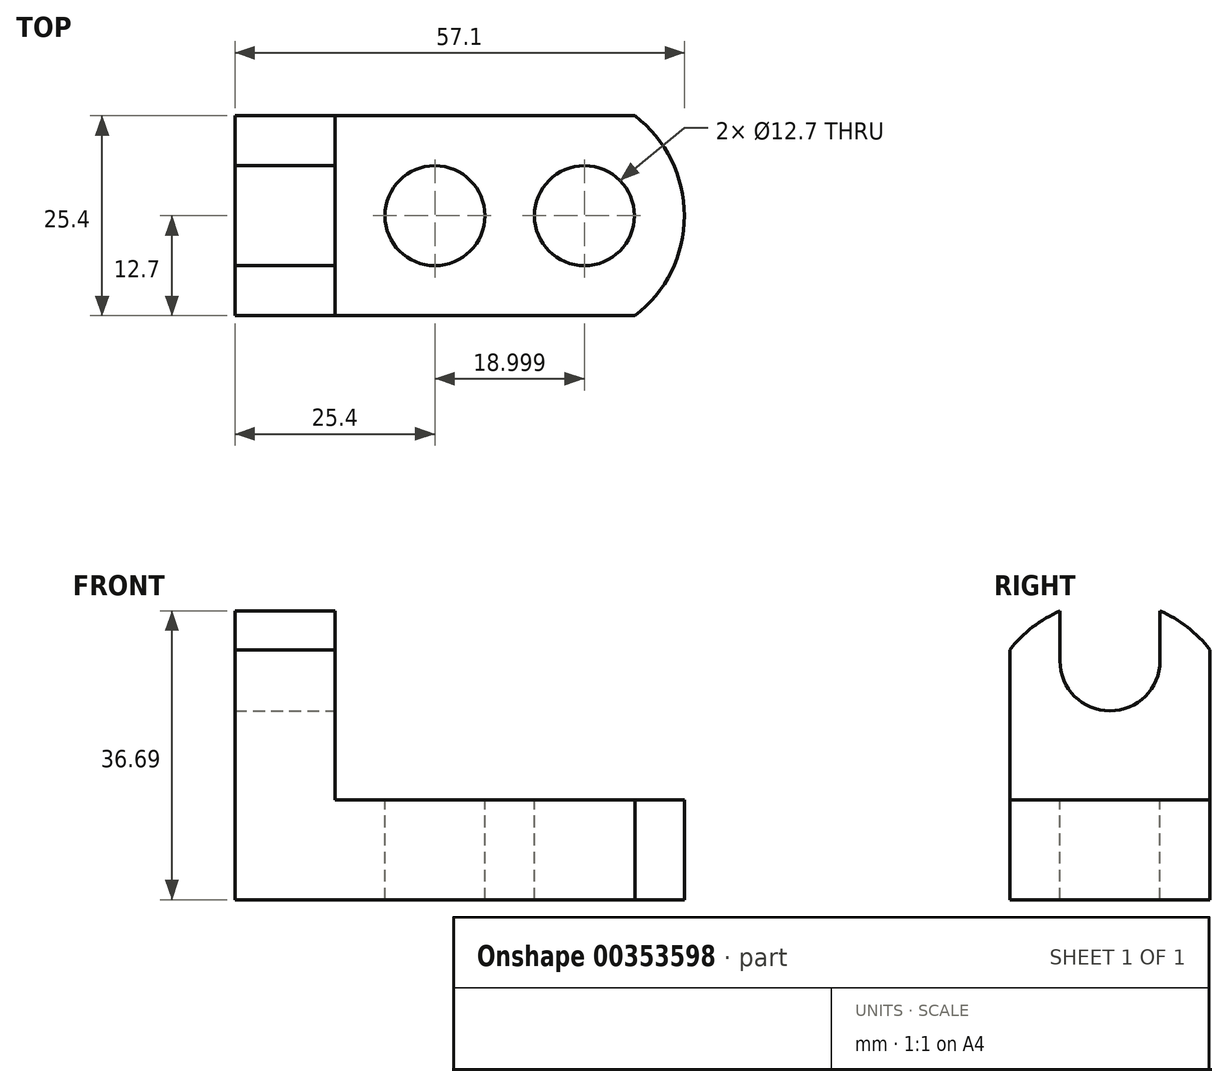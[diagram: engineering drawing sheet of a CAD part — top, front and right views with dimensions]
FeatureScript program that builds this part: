
annotation { "Feature Type Name" : "Feature", "Feature Type Description" : "" }
export const myFeature = defineFeature(function(context is Context, id is Id, definition is map)
    precondition{}
    {
        {
            var Q0;
            Q0=qCreatedBy(makeId("Front.planeOp"),FACE);
            var sketch = newSketch(context, id + "F0", { "sketchPlane" : qUnion([Q0])});
            skLineSegment(sketch, "E0", {"start": v(0, 0) * mm, "end": v(0, 38.1) * mm});
            skLineSegment(sketch, "E1", {"start": v(0, 38.1) * mm, "end": v(12.7, 38.1) * mm});
            skLineSegment(sketch, "E2", {"start": v(12.7, 38.1) * mm, "end": v(12.7, 12.7) * mm});
            skLineSegment(sketch, "E3", {"start": v(12.7, 12.7) * mm, "end": v(57.15, 12.7) * mm});
            skLineSegment(sketch, "E4", {"start": v(57.15, 12.7) * mm, "end": v(57.15, 0) * mm});
            skLineSegment(sketch, "E5", {"start": v(57.15, 0) * mm, "end": v(0, 0) * mm});
            skSolve(sketch);
        }
        {
            var Q0;
            Q0=makeQuery(id+"F0.imprint","IMPRINT",FACE,{"disambiguationData":[TD([[makeQuery(id+"F0.imprint","IMPRINT",EDGE,{"derivedFrom":sQuery(id+"F0.wireOp",EDGE,"E0")}),-1.0]])]});
            extrude(context, id + "F1", {"entities" : qUnion([Q0]), "depth" : 25.4 * mm});
        }
        {
            var Q0;
            Q0=makeQuery(id+"F1.opExtrude","SWEPT_FACE",FACE,{"disambiguationData":[OSD([sQuery(id+"F0.wireOp",EDGE,"E2")])]});
            var sketch = newSketch(context, id + "F2", { "sketchPlane" : qUnion([Q0])});
            skLineSegment(sketch, "E6", {"start": v(-25.4, 31.75) * mm, "end": v(-25.4, 38.1) * mm});
            skLineSegment(sketch, "E7", {"start": v(-25.4, 38.1) * mm, "end": v(0, 38.1) * mm});
            skLineSegment(sketch, "E8", {"start": v(0, 38.1) * mm, "end": v(0, 31.75) * mm});
            skArc(sketch, "E9", {"start": v(0, 31.75) * mm, "mid": v(-12.7, 38) * mm, "end": v(-25.4, 31.75) * mm});
            skSolve(sketch);
        }
        {
            var Q0;
            Q0=makeQuery(id+"F2.imprint","IMPRINT",FACE,{"disambiguationData":[TD([[makeQuery(id+"F2.imprint","IMPRINT",EDGE,{"derivedFrom":sQuery(id+"F2.wireOp",EDGE,"E6")}),1.0]])]});
            extrude(context, id + "F3", {"entities" : qUnion([Q0]), "operationType" : NewBodyOperationType.REMOVE, "oppositeDirection" : true, "depth" : 25.4 * mm});
        }
        {
            var Q0;
            Q0=makeQuery(id+"F1.opExtrude","SWEPT_FACE",FACE,{"disambiguationData":[OSD([sQuery(id+"F0.wireOp",EDGE,"E2")])]});
            var sketch = newSketch(context, id + "F4", { "sketchPlane" : qUnion([Q0])});
            skLineSegment(sketch, "E10", {"start": v(-19.05, 36.69) * mm, "end": v(-19.05, 30.34) * mm});
            skLineSegment(sketch, "E11", {"start": v(-6.35, 36.69) * mm, "end": v(-6.35, 30.34) * mm});
            skArc(sketch, "E12", {"start": v(-19.05, 30.34) * mm, "mid": v(-12.7, 23.99) * mm, "end": v(-6.35, 30.34) * mm});
            skSolve(sketch);
        }
        {
            var Q0;
            {var subQ0=sQuery(id+"F4.wireOp",EDGE,"E10");Q0=makeQuery(id+"F4.imprint","IMPRINT",FACE,{"disambiguationData":[TD([[makeQuery(id+"F4.imprint","IMPRINT",EDGE,{"derivedFrom":subQ0}),1.0]])]});}
            extrude(context, id + "F5", {"entities" : qUnion([Q0]), "operationType" : NewBodyOperationType.REMOVE, "oppositeDirection" : true, "depth" : 25.4 * mm});
        }
        {
            var Q0;
            Q0=makeQuery(id+"F1.opExtrude","SWEPT_FACE",FACE,{"disambiguationData":[OSD([sQuery(id+"F0.wireOp",EDGE,"E3")])]});
            var sketch = newSketch(context, id + "F6", { "sketchPlane" : qUnion([Q0])});
            skLineSegment(sketch, "E13", {"start": v(50.8, 0) * mm, "end": v(57.15, 0) * mm});
            skLineSegment(sketch, "E14", {"start": v(57.15, 0) * mm, "end": v(57.15, -25.4) * mm});
            skLineSegment(sketch, "E15", {"start": v(57.15, -25.4) * mm, "end": v(50.8, -25.4) * mm});
            skArc(sketch, "E16", {"start": v(50.8, -25.4) * mm, "mid": v(57.1, -12.7) * mm, "end": v(50.8, 0) * mm});
            skSolve(sketch);
        }
        {
            var Q0;
            Q0=makeQuery(id+"F6.imprint","IMPRINT",FACE,{"disambiguationData":[TD([[makeQuery(id+"F6.imprint","IMPRINT",EDGE,{"derivedFrom":sQuery(id+"F6.wireOp",EDGE,"E13")}),-1.0]])]});
            extrude(context, id + "F7", {"entities" : qUnion([Q0]), "operationType" : NewBodyOperationType.REMOVE, "oppositeDirection" : true, "depth" : 25.4 * mm});
        }
        {
            var Q0;
            Q0=makeQuery(id+"F1.opExtrude","SWEPT_FACE",FACE,{"disambiguationData":[OSD([sQuery(id+"F0.wireOp",EDGE,"E3")])]});
            var sketch = newSketch(context, id + "F8", { "sketchPlane" : qUnion([Q0])});
            skCircle(sketch, "E17", {"center": v(25.4, -12.7) * mm, "radius": 6.35 * mm});
            skCircle(sketch, "E18", {"center": v(44.4, -12.7) * mm, "radius": 6.35 * mm});
            skSolve(sketch);
        }
        {
            var Q0;
            Q0=makeQuery(id+"F8.imprint","IMPRINT",FACE,{"disambiguationData":[TD([[makeQuery(id+"F8.imprint","IMPRINT",EDGE,{"derivedFrom":sQuery(id+"F8.wireOp",EDGE,"E17")}),1.0]])]});
            var Q1;
            Q1=makeQuery(id+"F8.imprint","IMPRINT",FACE,{"disambiguationData":[TD([[makeQuery(id+"F8.imprint","IMPRINT",EDGE,{"derivedFrom":sQuery(id+"F8.wireOp",EDGE,"E18")}),1.0]])]});
            extrude(context, id + "F9", {"entities" : qUnion([Q0, Q1]), "operationType" : NewBodyOperationType.REMOVE, "oppositeDirection" : true, "depth" : 25.4 * mm});
        }
    });
